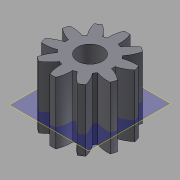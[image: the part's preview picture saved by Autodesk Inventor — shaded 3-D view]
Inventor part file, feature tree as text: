
AUTODESK INVENTOR PART (.ipt)
format: ipt  version: 2015 (Build 190159000, 159)  size: 166,912 bytes
history: native  units: in
note: dims shown in document units (in); Inventor stores cm internally (conversion verified against a paired STEP export)
features: other x13, sketch x3, plane x2
ambient origin geometry x8: Origin, YZ Plane, XZ Plane, XY Plane, X Axis, Y Axis, Z Axis, Center Point
bodies: Solid1 (feature_tree)
feature tree (18):
  other  "Spur Gear1"
  other  "Solid1::Spur Gear1"
  other  "TaggingFeature1"
  sketch  "Sketch1"  dims[d0=0.3937in]
  sketch  "Sketch2"  dims[d16=0.4724in d17=0.0in d41=0.0in d43=0.4724in d46=0.4724in d47=0.0in d48=0.0in]
  sketch  "Sketch3"
  plane  "XZ Plane_1"
  plane  "Work Plane2"
  other  "Z Axis_1"
  other  "Srf1"
  other  "Srf1::Derived"
  other  "Distance iMate"
  other  "Align iMate"
  other  "Mesh iMate"
  other  "Axis iMate"
  other  "Position iMate"
  other  "Mesh iMate2"
  other  "Start plane iMate"
